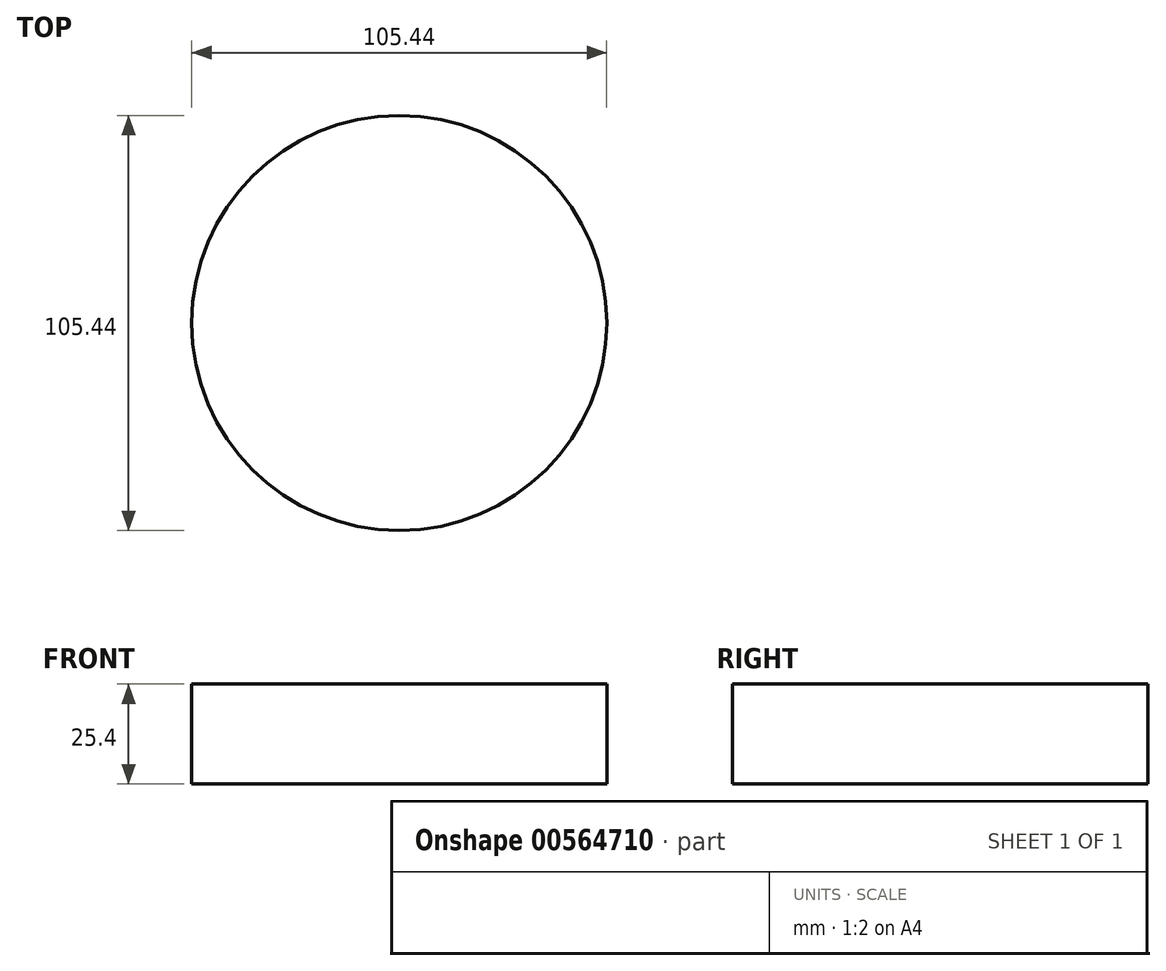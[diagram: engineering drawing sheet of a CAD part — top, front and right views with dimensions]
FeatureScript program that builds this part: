
annotation { "Feature Type Name" : "Feature", "Feature Type Description" : "" }
export const myFeature = defineFeature(function(context is Context, id is Id, definition is map)
    precondition{}
    {
        {
            var Q0;
            Q0=qCreatedBy(makeId("Top.planeOp"),FACE);
            var sketch = newSketch(context, id + "F0", { "sketchPlane" : qUnion([Q0])});
            skCircle(sketch, "E0", {"center": v(0, 0) * mm, "radius": 52.72 * mm});
            skSolve(sketch);
        }
        {
            var Q0;
            Q0=sQuery(id+"F0.wireOp",EDGE,"E0");
            extrude(context, id + "F1", {"bodyType" : ToolBodyType.SURFACE, "surfaceEntities" : qUnion([Q0]), "depth" : 25.4 * mm, "offsetDistance" : 25.4 * mm});
        }
    });
